# Revit family: Illustris plastic range_191 PX
name_source: partatom
category: Electrical Fixtures
revit_build: Autodesk Revit 2018 (Build: 20170223_1515(x64)
units: mm (PartAtom-declared; Revit-internal decimal feet)

## family parameters
Always vertical = Yes
Cut with Voids When Loaded = No
Maintain Annotation Orientation = No
Part Type = Normal
Room Calculation Point = No
Round Connector Dimension = Use Diameter
Shared = No
Work Plane-Based = Yes

## types (1)
- Scene Control - Plastic - Black/White
    Ambient temperature = 0 °C to +50 °C
    Cable rating = All cables must be mains rated.
    DALI Standard = IEC 62386 (Part 209: CT and x-y control only)
    DALI cable = Push-fit terminals. Wire section: 0.5 mm² – 1.5 mm² solid or stranded.
    DALI consumption = Typical: 22 mA @ 16 V Maximum: 40 mA @ 9.5 V
    DALI supply input = 9.5 V – 22.5 V
    Default Elevation = 0 mm  [stored 0 ft]
    Designer: = 5.3.0 or later for standard panels 5.4.3 for custom panels
    Dimensions: = 89 mm × 89 mm 
290x: 89 mm × 89 mm
    EMC = EN 55015
 EN 61547
    Environment: = Complies with WEEE and RoHS directives.
    FCC = Contains FCC ID: WAP2005.
    IP code: = IP30
    Manufacturer = Helvar
    Material = Acrylic (PMMA)
 290x: Flame-retardant PC/ABS
    Model = 191PB/191PW
    RED = EN 300328 
EN 301489-17
    Relative humidity = Max. 90 %, noncondensing
    Safety = 60669-2-1
    Storage temperature = –10 °C to +70 °C
    Toolbox: = 2.3.7 or later (custom panels not supported)
    Weight: = 90 g 
290x: 50 g
    Wireless connectivity = Bluetooth® Smart™

note: [stored X ft] marks values corroborated as IEEE doubles in the binary element streams (Revit-internal decimal feet)

## geometry (parser evidence)
native form markers: Sweep x5
no freeform markers — native parametric forms only
